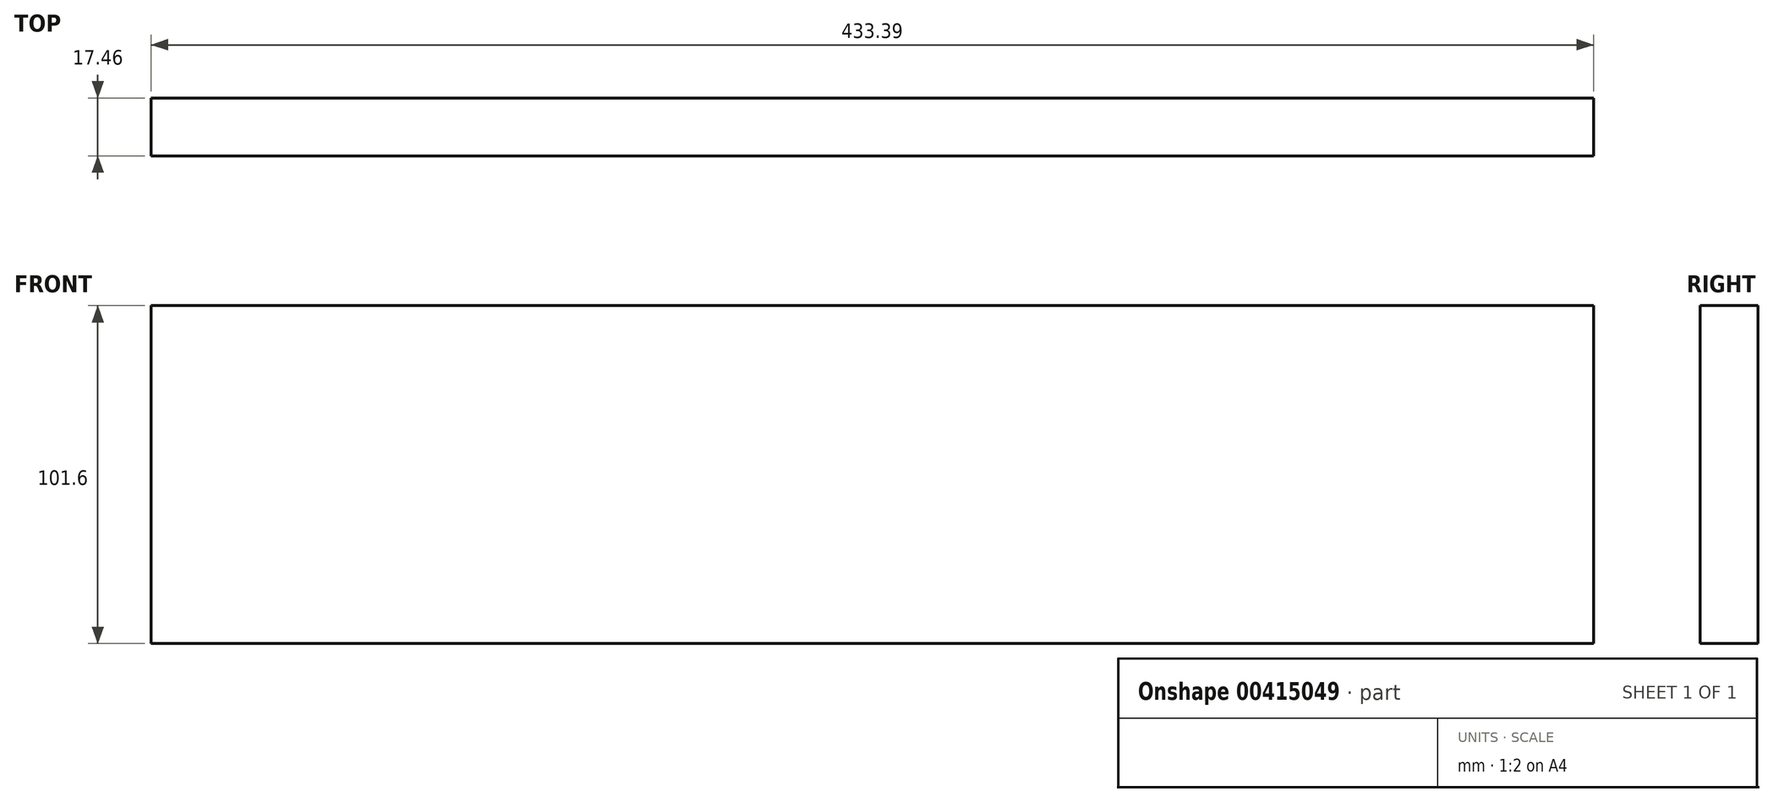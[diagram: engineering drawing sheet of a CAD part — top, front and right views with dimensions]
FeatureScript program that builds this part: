
annotation { "Feature Type Name" : "Feature", "Feature Type Description" : "" }
export const myFeature = defineFeature(function(context is Context, id is Id, definition is map)
    precondition{}
    {
        {
            var Q0;
            Q0=qCreatedBy(makeId("Front.planeOp"),FACE);
            var sketch = newSketch(context, id + "F0", { "sketchPlane" : qUnion([Q0])});
            skLineSegment(sketch, "E0.bottom", {"start": v(0, 0) * mm, "end": v(433.39, 0) * mm});
            skLineSegment(sketch, "E0.top", {"start": v(0, 101.6) * mm, "end": v(433.39, 101.6) * mm});
            skLineSegment(sketch, "E0.left", {"start": v(0, 0) * mm, "end": v(0, 101.6) * mm});
            skLineSegment(sketch, "E0.right", {"start": v(433.39, 0) * mm, "end": v(433.39, 101.6) * mm});
            skSolve(sketch);
        }
        {
            var Q0;
            Q0=makeQuery(id+"F0.imprint","IMPRINT",FACE,{"disambiguationData":[TD([[makeQuery(id+"F0.imprint","IMPRINT",EDGE,{"derivedFrom":sQuery(id+"F0.wireOp",EDGE,"E0.bottom")}),1.0]])]});
            extrude(context, id + "F1", {"entities" : qUnion([Q0]), "depth" : 17.46 * mm, "offsetDistance" : 25.4 * mm});
        }
    });
